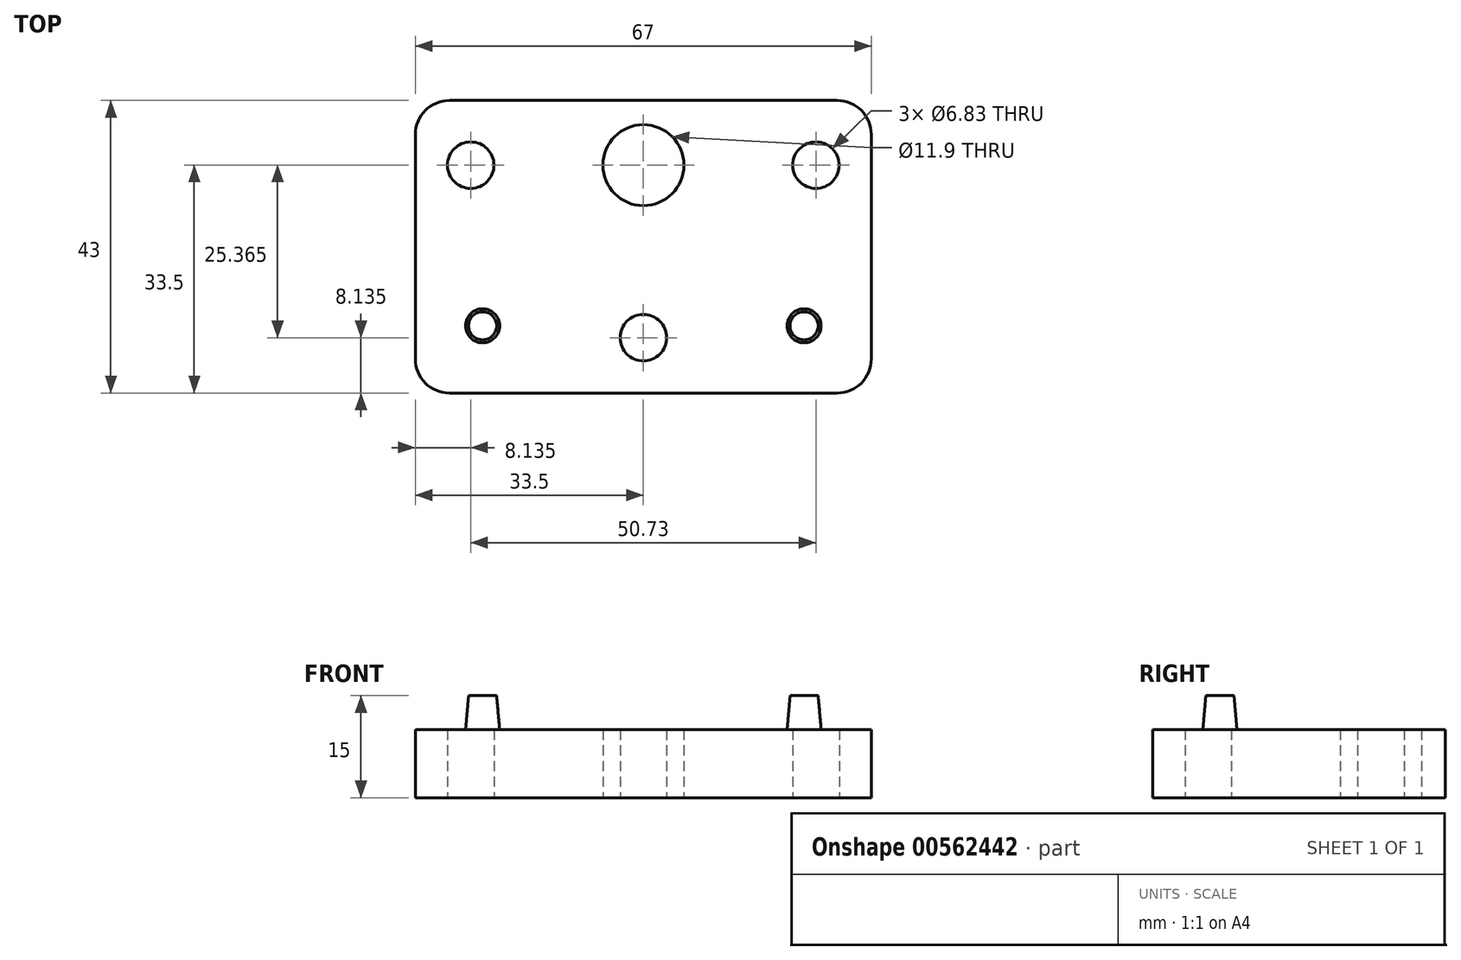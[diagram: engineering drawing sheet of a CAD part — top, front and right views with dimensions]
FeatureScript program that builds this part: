
annotation { "Feature Type Name" : "Feature", "Feature Type Description" : "" }
export const myFeature = defineFeature(function(context is Context, id is Id, definition is map)
    precondition{}
    {
        {
            var Q0;
            Q0=qCreatedBy(makeId("Top.planeOp"),FACE);
            var sketch = newSketch(context, id + "F0", { "sketchPlane" : qUnion([Q0])});
            skLineSegment(sketch, "E0.bottom", {"start": v(-33.5, 9.5) * mm, "end": v(33.5, 9.5) * mm});
            skLineSegment(sketch, "E0.top", {"start": v(-33.5, -33.5) * mm, "end": v(33.5, -33.5) * mm});
            skLineSegment(sketch, "E0.left", {"start": v(-33.5, 9.5) * mm, "end": v(-33.5, -33.5) * mm});
            skLineSegment(sketch, "E0.right", {"start": v(33.5, 9.5) * mm, "end": v(33.5, -33.5) * mm});
            skCircle(sketch, "E1", {"center": v(0, 0) * mm, "radius": 5.95 * mm});
            skCircle(sketch, "E2", {"center": v(25.37, 0) * mm, "radius": 3.42 * mm});
            skCircle(sketch, "E3", {"center": v(-25.37, 0) * mm, "radius": 3.42 * mm});
            skLineSegment(sketch, "E4.bottom", {"start": v(-14.98, 9.5) * mm, "end": v(14.98, 9.5) * mm});
            skLineSegment(sketch, "E4.top", {"start": v(-14.98, -33.5) * mm, "end": v(14.98, -33.5) * mm});
            skLineSegment(sketch, "E4.left", {"start": v(-14.98, 9.5) * mm, "end": v(-14.98, -33.5) * mm});
            skLineSegment(sketch, "E4.right", {"start": v(14.98, 9.5) * mm, "end": v(14.98, -33.5) * mm});
            skCircle(sketch, "E5", {"center": v(-25.37, 0) * mm, "radius": 5.42 * mm});
            skCircle(sketch, "E6", {"center": v(25.37, 0) * mm, "radius": 5.42 * mm});
            skCircle(sketch, "E7", {"center": v(0, -25.37) * mm, "radius": 3.42 * mm});
            skCircle(sketch, "E8", {"center": v(0, -25.37) * mm, "radius": 5.42 * mm});
            skSolve(sketch);
        }
        {
            var Q0;
            Q0=makeQuery(id+"F0.imprint","IMPRINT",FACE,{"disambiguationData":[TD([[makeQuery(id+"F0.imprint","IMPRINT",EDGE,{"derivedFrom":sQuery(id+"F0.wireOp",EDGE,"E1")}),-1.0]])]});
            extrude(context, id + "F1", {"entities" : qUnion([Q0]), "depth" : 10 * mm});
        }
        {
            var Q0;
            {var subQ1=sQuery(id+"F0.wireOp",EDGE,"E0.left");Q0=makeQuery(id+"F0.imprint","IMPRINT",FACE,{"disambiguationData":[TD([[makeQuery(id+"F0.imprint","IMPRINT",EDGE,{"derivedFrom":subQ1}),1.0]])]});}
            var Q1;
            {var subQ1=sQuery(id+"F0.wireOp",EDGE,"E0.right");Q1=makeQuery(id+"F0.imprint","IMPRINT",FACE,{"disambiguationData":[TD([[makeQuery(id+"F0.imprint","IMPRINT",EDGE,{"derivedFrom":subQ1}),-1.0]])]});}
            extrude(context, id + "F2", {"entities" : qUnion([Q0, Q1]), "operationType" : NewBodyOperationType.ADD, "depth" : 10 * mm});
        }
        {
            var Q0;
            Q0=makeQuery(id+"F0.imprint","IMPRINT",FACE,{"disambiguationData":[TD([[makeQuery(id+"F0.imprint","IMPRINT",EDGE,{"derivedFrom":sQuery(id+"F0.wireOp",EDGE,"E3")}),-1.0]])]});
            var Q1;
            Q1=makeQuery(id+"F0.imprint","IMPRINT",FACE,{"disambiguationData":[TD([[makeQuery(id+"F0.imprint","IMPRINT",EDGE,{"derivedFrom":sQuery(id+"F0.wireOp",EDGE,"E2")}),-1.0]])]});
            var Q2;
            Q2=makeQuery(id+"F0.imprint","IMPRINT",FACE,{"disambiguationData":[TD([[makeQuery(id+"F0.imprint","IMPRINT",EDGE,{"derivedFrom":sQuery(id+"F0.wireOp",EDGE,"E7")}),-1.0]])]});
            extrude(context, id + "F3", {"entities" : qUnion([Q0, Q1, Q2]), "operationType" : NewBodyOperationType.ADD, "depth" : 10 * mm});
        }
        {
            var Q0;
            {var subQ0=sQuery(id+"F0.wireOp",EDGE,"E4.right");Q0=makeQuery(id+"F0.imprint","IMPRINT",FACE,{"disambiguationData":[TD([[makeQuery(id+"F0.imprint","IMPRINT",EDGE,{"derivedFrom":subQ0}),1.0]])]});}
            var Q1;
            {var subQ0=sQuery(id+"F0.wireOp",EDGE,"E4.left");Q1=makeQuery(id+"F0.imprint","IMPRINT",FACE,{"disambiguationData":[TD([[makeQuery(id+"F0.imprint","IMPRINT",EDGE,{"derivedFrom":subQ0}),-1.0]])]});}
            extrude(context, id + "F4", {"entities" : qUnion([Q0, Q1]), "operationType" : NewBodyOperationType.ADD, "depth" : 10 * mm});
        }
        {
            var Q0;
            Q0=qCreatedBy(makeId("Top.planeOp"),FACE);
            var sketch = newSketch(context, id + "F5", { "sketchPlane" : qUnion([Q0])});
            skLineSegment(sketch, "E9.rect.bottom", {"start": v(-28.11, 28.11) * mm, "end": v(28.12, 28.11) * mm});
            skLineSegment(sketch, "E9.rect.top", {"start": v(-28.12, -28.11) * mm, "end": v(28.11, -28.11) * mm});
            skLineSegment(sketch, "E9.rect.left", {"start": v(-28.11, 28.12) * mm, "end": v(-28.12, -28.11) * mm});
            skLineSegment(sketch, "E9.rect.right", {"start": v(28.12, 28.12) * mm, "end": v(28.11, -28.11) * mm});
            skPoint(sketch, "E9.rect.middle", {"position": v(0, 0) * mm});
            skCircle(sketch, "E10", {"center": v(0, 0) * mm, "radius": 19.04 * mm});
            skCircle(sketch, "E11", {"center": v(0, 0) * mm, "radius": 3.98 * mm});
            skCircle(sketch, "E12", {"center": v(-23.62, 23.62) * mm, "radius": 2.5 * mm});
            skCircle(sketch, "E13", {"center": v(23.62, 23.62) * mm, "radius": 2.5 * mm});
            skCircle(sketch, "E14", {"center": v(23.62, -23.62) * mm, "radius": 2.5 * mm});
            skCircle(sketch, "E15", {"center": v(-23.62, -23.62) * mm, "radius": 2.5 * mm});
            skLineSegment(sketch, "E16.rect.bottom", {"start": v(-23.62, 23.62) * mm, "end": v(23.62, 23.62) * mm, "construction": true});
            skLineSegment(sketch, "E16.rect.top", {"start": v(-23.62, -23.62) * mm, "end": v(23.62, -23.62) * mm, "construction": true});
            skLineSegment(sketch, "E16.rect.left", {"start": v(-23.62, 23.62) * mm, "end": v(-23.62, -23.62) * mm, "construction": true});
            skLineSegment(sketch, "E16.rect.right", {"start": v(23.62, 23.62) * mm, "end": v(23.62, -23.62) * mm, "construction": true});
            skCircle(sketch, "E17", {"center": v(0, 0) * mm, "radius": 5.38 * mm});
            skSolve(sketch);
        }
        {
            var Q0;
            {var subQ0=sQuery(id+"F0.wireOp",EDGE,"E8");var subQ1=sQuery(id+"F0.wireOp",EDGE,"E5");var subQ2=sQuery(id+"F0.wireOp",EDGE,"E6");var subQ3=sQuery(id+"F0.wireOp",EDGE,"E4.right");var subQ4=sQuery(id+"F0.wireOp",EDGE,"E0.top");var subQ5=sQuery(id+"F0.wireOp",EDGE,"E0.bottom");var subQ6=sQuery(id+"F0.wireOp",EDGE,"E4.left");Q0=makeQuery(id+"F3.boolean.opBoolean","MERGE",FACE,{"derivedFrom":[makeQuery(id+"F2.boolean.opBoolean","MERGE",FACE,{"derivedFrom":[makeQuery(id+"F1.opExtrude","CAP_FACE",FACE,{"disambiguationData":[OSD([sQuery(id+"F0.wireOp",EDGE,"E1"),sQuery(id+"F0.wireOp",EDGE,"E4.bottom"),sQuery(id+"F0.wireOp",EDGE,"E4.top"),subQ6,subQ3,subQ0])],"isStart":false}),makeQuery(id+"F2.opExtrude","CAP_FACE",FACE,{"disambiguationData":[OSD([subQ5,subQ4,sQuery(id+"F0.wireOp",EDGE,"E0.left"),subQ6,subQ1])],"isStart":false}),makeQuery(id+"F2.opExtrude","CAP_FACE",FACE,{"disambiguationData":[OSD([subQ5,subQ4,sQuery(id+"F0.wireOp",EDGE,"E0.right"),subQ3,subQ2])],"isStart":false})]}),makeQuery(id+"F3.opExtrude","CAP_FACE",FACE,{"disambiguationData":[OSD([sQuery(id+"F0.wireOp",EDGE,"E2"),subQ2])],"isStart":false}),makeQuery(id+"F3.opExtrude","CAP_FACE",FACE,{"disambiguationData":[OSD([sQuery(id+"F0.wireOp",EDGE,"E3"),subQ1])],"isStart":false}),makeQuery(id+"F3.opExtrude","CAP_FACE",FACE,{"disambiguationData":[OSD([sQuery(id+"F0.wireOp",EDGE,"E7"),subQ0])],"isStart":false})]});}
            var sketch = newSketch(context, id + "F6", { "sketchPlane" : qUnion([Q0])});
            skCircle(sketch, "E18", {"center": v(-23.62, -23.62) * mm, "radius": 2.5 * mm});
            skCircle(sketch, "E19", {"center": v(23.62, -23.62) * mm, "radius": 2.5 * mm});
            skSolve(sketch);
        }
        {
            var Q0;
            Q0=qSketchRegion(id+"F6",true);
            extrude(context, id + "F7", {"entities" : qUnion([Q0]), "operationType" : NewBodyOperationType.ADD, "depth" : 5 * mm, "hasDraft" : true, "draftAngle" : 5 * degree, "draftPullDirection" : true});
        }
        {
            var Q0;
            Q0=makeQuery(id+"F2.opExtrude","SWEPT_EDGE",EDGE,{"disambiguationData":[OSD([sQuery(id+"F0.wireOp",EDGE,"E0.top"),sQuery(id+"F0.wireOp",EDGE,"E0.left")])]});
            var Q1;
            Q1=makeQuery(id+"F2.opExtrude","SWEPT_EDGE",EDGE,{"disambiguationData":[OSD([sQuery(id+"F0.wireOp",EDGE,"E0.top"),sQuery(id+"F0.wireOp",EDGE,"E0.right")])]});
            var Q2;
            Q2=makeQuery(id+"F2.opExtrude","SWEPT_EDGE",EDGE,{"disambiguationData":[OSD([sQuery(id+"F0.wireOp",EDGE,"E0.bottom"),sQuery(id+"F0.wireOp",EDGE,"E0.right")])]});
            var Q3;
            Q3=makeQuery(id+"F2.opExtrude","SWEPT_EDGE",EDGE,{"disambiguationData":[OSD([sQuery(id+"F0.wireOp",EDGE,"E0.bottom"),sQuery(id+"F0.wireOp",EDGE,"E0.left")])]});
            fillet(context, id + "F8", {"entities" : qUnion([Q0, Q1, Q2, Q3]), "radius" : 5 * mm, "tangentPropagation" : true, "allowEdgeOverflow" : false});
        }
    });
